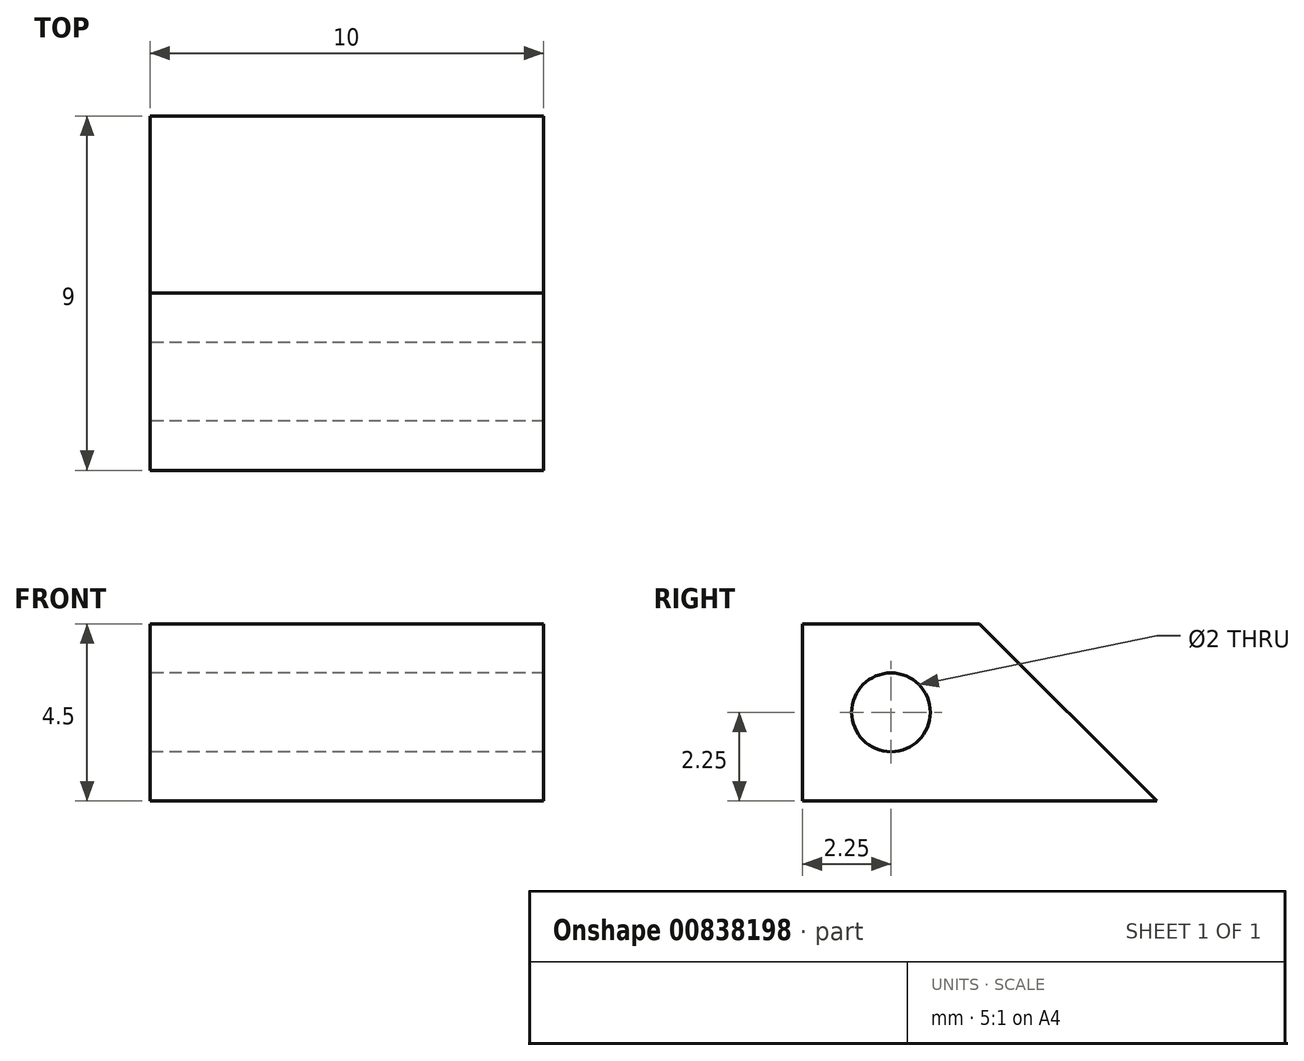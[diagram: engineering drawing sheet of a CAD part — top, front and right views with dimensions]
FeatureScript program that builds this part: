
annotation { "Feature Type Name" : "Feature", "Feature Type Description" : "" }
export const myFeature = defineFeature(function(context is Context, id is Id, definition is map)
    precondition{}
    {
        {
            var Q0;
            Q0=qCreatedBy(makeId("Right.planeOp"),FACE);
            var sketch = newSketch(context, id + "F0", { "sketchPlane" : qUnion([Q0])});
            skLineSegment(sketch, "E0", {"start": v(0, 0) * mm, "end": v(9, 0) * mm});
            skLineSegment(sketch, "E1", {"start": v(0, 0) * mm, "end": v(0, 4.5) * mm});
            skLineSegment(sketch, "E2", {"start": v(0, 4.5) * mm, "end": v(4.5, 4.5) * mm});
            skLineSegment(sketch, "E3", {"start": v(4.5, 0) * mm, "end": v(4.5, 4.5) * mm});
            skLineSegment(sketch, "E4", {"start": v(4.5, 4.5) * mm, "end": v(9, 0) * mm});
            skLineSegment(sketch, "E5", {"start": v(4.5, 4.5) * mm, "end": v(0, 0) * mm, "construction": true});
            skLineSegment(sketch, "E6", {"start": v(0, 4.5) * mm, "end": v(4.5, 0) * mm, "construction": true});
            skCircle(sketch, "E7", {"center": v(2.25, 2.25) * mm, "radius": 1 * mm});
            skCircle(sketch, "E8", {"center": v(2.25, 2.25) * mm, "radius": 1.9 * mm});
            skLineSegment(sketch, "E9", {"start": v(6.75, 2.25) * mm, "end": v(4.5, 0) * mm, "construction": true});
            skSolve(sketch);
        }
        {
            var Q0;
            Q0=qCreatedBy(makeId("Right.planeOp"),FACE);
            var sketch = newSketch(context, id + "F1", { "sketchPlane" : qUnion([Q0])});
            skLineSegment(sketch, "E10", {"start": v(9, 0) * mm, "end": v(13.5, 0) * mm});
            skLineSegment(sketch, "E11", {"start": v(13.5, 0) * mm, "end": v(13.5, 4.5) * mm});
            skLineSegment(sketch, "E12", {"start": v(13.5, 4.5) * mm, "end": v(9, 4.5) * mm});
            skLineSegment(sketch, "E13", {"start": v(9, 4.5) * mm, "end": v(9, 0) * mm});
            skLineSegment(sketch, "E14", {"start": v(9, 0) * mm, "end": v(13.5, 4.5) * mm, "construction": true});
            skLineSegment(sketch, "E15", {"start": v(13.5, 0) * mm, "end": v(9, 4.5) * mm, "construction": true});
            skCircle(sketch, "E16", {"center": v(11.25, 2.25) * mm, "radius": 1 * mm});
            skLineSegment(sketch, "E17", {"start": v(9, 4.5) * mm, "end": v(4.5, 4.5) * mm});
            skLineSegment(sketch, "E18", {"start": v(9, 0) * mm, "end": v(4.5, 4.5) * mm});
            skLineSegment(sketch, "E19", {"start": v(6.75, 2.25) * mm, "end": v(9, 4.5) * mm, "construction": true});
            skPoint(sketch, "E20.orphan", {"position": v(0, 0) * mm});
            skSolve(sketch);
        }
        {
            var Q0;
            {var subQ2=sQuery(id+"F0.wireOp",EDGE,"E3");Q0=makeQuery(id+"F0.imprint","IMPRINT",FACE,{"disambiguationData":[TD([[makeQuery(id+"F0.imprint","IMPRINT",EDGE,{"derivedFrom":subQ2}),-1.0]])]});}
            var Q1;
            {var subQ1=sQuery(id+"F0.wireOp",EDGE,"E1");Q1=makeQuery(id+"F0.imprint","IMPRINT",FACE,{"disambiguationData":[TD([[makeQuery(id+"F0.imprint","IMPRINT",EDGE,{"derivedFrom":subQ1}),-1.0]])]});}
            var Q2;
            Q2=makeQuery(id+"F0.imprint","IMPRINT",FACE,{"disambiguationData":[TD([[makeQuery(id+"F0.imprint","IMPRINT",EDGE,{"derivedFrom":sQuery(id+"F0.wireOp",EDGE,"E7")}),-1.0]])]});
            var Q3;
            Q3=sQuery(id+"F0.wireOp",EDGE,"E1");
            var Q4;
            Q4=sQuery(id+"F0.wireOp",EDGE,"E2");
            var Q5;
            Q5=sQuery(id+"F1.wireOp",EDGE,"E18");
            var Q6;
            Q6=sQuery(id+"F0.wireOp",EDGE,"E0");
            extrude(context, id + "F2", {"entities" : qUnion([Q0, Q1, Q2]), "surfaceEntities" : qUnion([Q3, Q4, Q5, Q6]), "depth" : 10 * mm, "offsetDistance" : 25 * mm});
        }
    });
